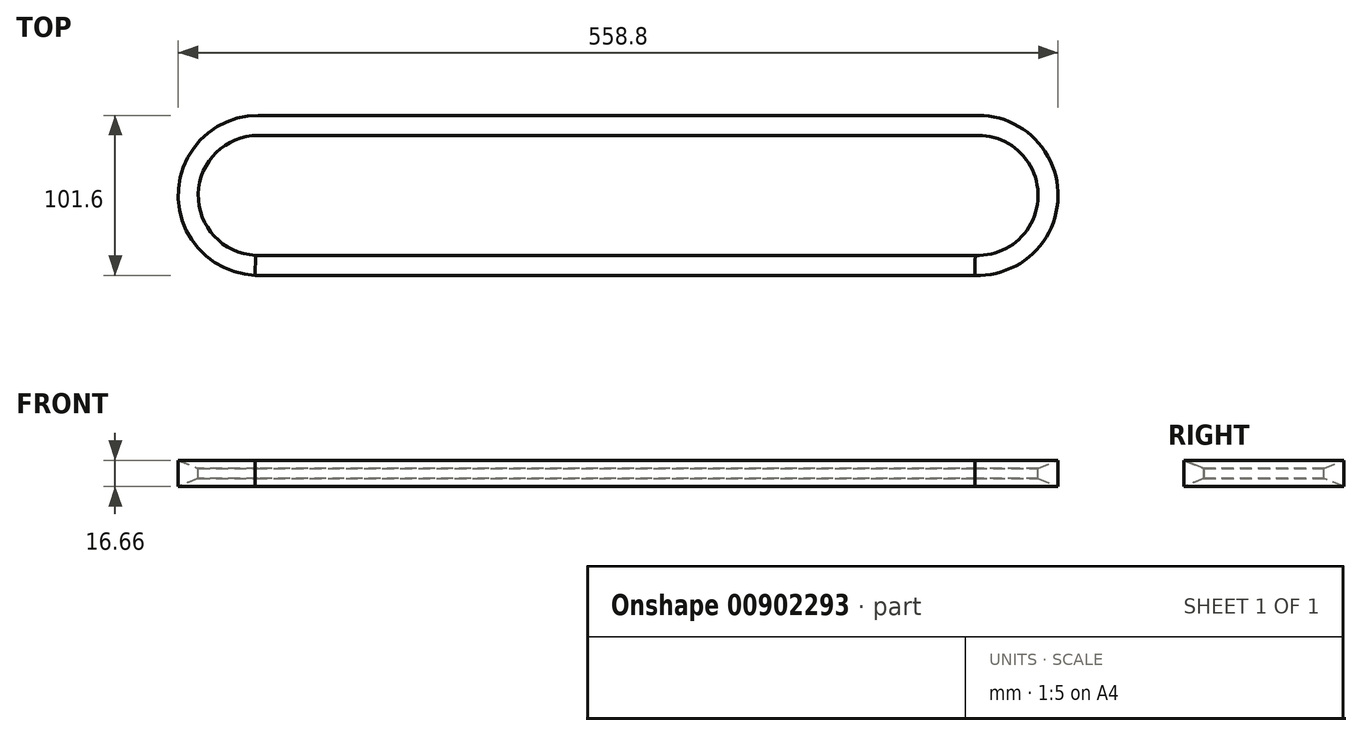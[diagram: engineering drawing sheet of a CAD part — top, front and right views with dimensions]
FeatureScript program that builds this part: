
annotation { "Feature Type Name" : "Feature", "Feature Type Description" : "" }
export const myFeature = defineFeature(function(context is Context, id is Id, definition is map)
    precondition{}
    {
        {
            var Q0;
            Q0=qCreatedBy(makeId("Top.planeOp"),FACE);
            var sketch = newSketch(context, id + "F0", { "sketchPlane" : qUnion([Q0])});
            skArc(sketch, "E0", {"start": v(369.13, -38.06) * mm, "mid": v(409, -0.9) * mm, "end": v(370.9, 38.1) * mm});
            skArc(sketch, "E1", {"start": v(-86.3, 38.1) * mm, "mid": v(-124.38, 0.9) * mm, "end": v(-88.07, -38.06) * mm});
            skLineSegment(sketch, "E2", {"start": v(-86.3, 38.1) * mm, "end": v(370.9, 38.1) * mm});
            skLineSegment(sketch, "E3", {"start": v(369.13, -38.06) * mm, "end": v(-88.07, -38.06) * mm});
            skLineSegment(sketch, "E4", {"start": v(370.9, 38.1) * mm, "end": v(370.9, 0) * mm});
            skLineSegment(sketch, "E5", {"start": v(370.9, 0) * mm, "end": v(409, 0) * mm});
            skSolve(sketch);
        }
        {
            var Q0;
            Q0=sQuery(id+"F0.wireOp",EDGE,"E2");
            var Q1;
            Q1=sQuery(id+"F0.wireOp",VERTEX,"E2.end");
            cPlane(context, id + "F1", {"entities" : qUnion([Q0, Q1]), "cplaneType" : CPlaneType.CURVE_POINT, "offset" : 25.4 * mm, "width" : 152.4 * mm, "height" : 152.4 * mm});
        }
        {
            var Q0;
            Q0=qCreatedBy(id+"F1.planeOp",FACE);
            var sketch = newSketch(context, id + "F2", { "sketchPlane" : qUnion([Q0])});
            skLineSegment(sketch, "E6", {"start": v(38.1, 0) * mm, "end": v(38.1, 3.18) * mm});
            skLineSegment(sketch, "E7", {"start": v(50.8, 0) * mm, "end": v(38.1, 0) * mm});
            skLineSegment(sketch, "E8", {"start": v(38.1, 3.17) * mm, "end": v(50.8, 8.33) * mm});
            skLineSegment(sketch, "E9", {"start": v(50.8, 8.33) * mm, "end": v(50.8, 0) * mm});
            skLineSegment(sketch, "E10", {"start": v(50.8, 0) * mm, "end": v(50.8, -8.33) * mm});
            skLineSegment(sketch, "E11", {"start": v(50.8, -8.33) * mm, "end": v(38.1, -3.17) * mm});
            skLineSegment(sketch, "E12", {"start": v(38.1, -3.17) * mm, "end": v(38.1, 0) * mm});
            skSolve(sketch);
        }
        {
            var Q0;
            Q0=makeQuery(id+"F2.imprint","IMPRINT",FACE,{"disambiguationData":[TD([[makeQuery(id+"F2.imprint","IMPRINT",EDGE,{"derivedFrom":sQuery(id+"F2.wireOp",EDGE,"E6")}),-1.0]])]});
            var Q1;
            Q1=makeQuery(id+"F2.imprint","IMPRINT",FACE,{"disambiguationData":[TD([[makeQuery(id+"F2.imprint","IMPRINT",EDGE,{"derivedFrom":sQuery(id+"F2.wireOp",EDGE,"E7")}),1.0]])]});
            var Q2;
            Q2=sQuery(id+"F0.wireOp",EDGE,"E2");
            var Q3;
            Q3=sQuery(id+"F0.wireOp",EDGE,"E1");
            var Q4;
            Q4=sQuery(id+"F0.wireOp",EDGE,"E3");
            var Q5;
            Q5=sQuery(id+"F0.wireOp",EDGE,"E0");
            sweep(context, id + "F3", {"profiles" : qUnion([Q0, Q1]), "path" : qUnion([Q2, Q3, Q4, Q5])});
        }
    });
